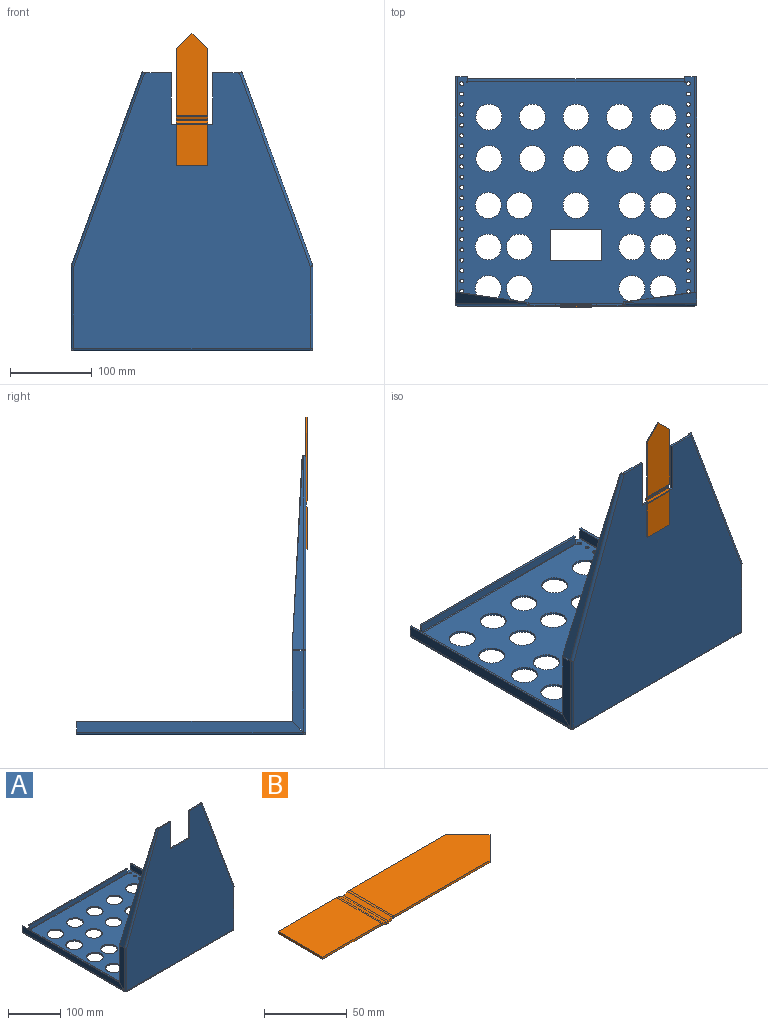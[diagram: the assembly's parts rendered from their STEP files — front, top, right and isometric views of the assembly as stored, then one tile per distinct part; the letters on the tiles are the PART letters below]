
ASSEMBLY  parts=2 mates=1
PART A: 171 faces, bbox 295.7x280.2x341.3 mm
  f0: plane 2.54x0.01mm, normal (0,1,0), area 0mm2, adj f15,f16,f26,f30
  f1: plane 2.54x0.01mm, normal (0,0,-1), area 0mm2, adj f30,f35,f36,f37
  f2: plane 2.54x0.01mm, normal (0,1,0), area 0mm2, adj f15,f16,f25,f31
  f3: plane 2.54x0.01mm, normal (0,0,-1), area 0mm2, adj f31,f34,f36,f37
  f4: plane 236.89x86.82mm, normal (-0.94,0,0.34), area 1788.3mm2, adj f6,f7,f97,f99,f170
  f5: plane 236.89x86.82mm, normal (0.94,0,-0.34), area 1788.3mm2, adj f6,f7,f98,f99,f170
  f6: plane 8.51x5.18mm, normal (0,1,0), area 20.6mm2, adj f4,f5,f99,f170
  f7: plane 2.39x0.87mm, normal (0.34,0,0.94), area 1.4mm2, adj f4,f5,f96,f170
  f8: plane 2.39x1.27mm, normal (-0.34,0,0.94), area 3.2mm2, adj f9,f10,f63,f169
  f9: plane 236.89x86.82mm, normal (0.94,0,0.34), area 1878.2mm2, adj f8,f11,f65,f67,f169
  f10: plane 236.89x86.82mm, normal (-0.94,0,-0.34), area 1878.2mm2, adj f8,f11,f66,f67,f169
  f11: plane 8.51x5.18mm, normal (0,1,0), area 20.6mm2, adj f9,f10,f67,f169
  f12: plane 337.08x289.1mm, normal (0,-1,0), area 73613.6mm2, adj f14,f18,f41,f43,f44,f45,f47,f48
  f13: plane 337.08x289.1mm, normal (0,1,0), area 73613.6mm2, adj f14,f18,f42,f43,f44,f45,f47,f48
  f14: plane 30.88x2.54mm, normal (0,0,1), area 78.4mm2, adj f12,f13,f45,f53
  f15: plane 289.1x276.89mm, normal (0,0,-1), area 57101.5mm2, adj f0,f2,f17,f19,f20,f21,f22,f23
  f16: plane 289.1x276.89mm, normal (0,0,1), area 57101.5mm2, adj f0,f2,f17,f19,f20,f21,f22,f23
  f17: plane 11.96x2.54mm, normal (0,1,0), area 30.4mm2, adj f15,f16,f21,f69
  f18: plane 30.88x2.54mm, normal (0,0,1), area 78.4mm2, adj f12,f13,f44,f48
  f19: plane 11.96x2.54mm, normal (0,1,0), area 30.4mm2, adj f15,f16,f20,f77
  f20: plane 5.08x2.54mm, normal (1,0,0), area 12.9mm2, adj f15,f16,f19,f22
  f21: plane 5.08x2.54mm, normal (-1,0,0), area 12.9mm2, adj f15,f16,f17,f29
  f22: plane 2.54x1.27mm, normal (0,-1,0), area 3.2mm2, adj f15,f16,f20,f23
  f23: plane 2.54x2.01mm, normal (1,0,0), area 5.1mm2, adj f15,f16,f22,f24
  f24: plane 2.54x1.27mm, normal (0,1,0), area 3.2mm2, adj f15,f16,f23,f25
  f25: plane 2.54x1.27mm, normal (-1,0,0), area 3.2mm2, adj f2,f15,f16,f24
  f26: plane 2.54x1.27mm, normal (1,0,0), area 3.2mm2, adj f0,f15,f16,f27
  f27: plane 2.54x1.27mm, normal (0,1,0), area 3.2mm2, adj f15,f16,f26,f28
  f28: plane 2.54x2.01mm, normal (-1,0,0), area 5.1mm2, adj f15,f16,f27,f29
  f29: plane 2.54x1.27mm, normal (0,-1,0), area 3.2mm2, adj f15,f16,f21,f28
  f30: plane 3.28x3.28mm, normal (1,0,0), area 8mm2, adj f0,f1,f32,f33
  f31: plane 3.28x3.28mm, normal (-1,0,0), area 8mm2, adj f2,f3,f32,f33
  f32: cylinder r=3.28mm len=265.16mm, axis (-1,0,0), area 1364.7mm2, adj f15,f30,f31,f36
  f33: cylinder r=0.74mm len=265.16mm, axis (-1,0,0), area 306.8mm2, adj f16,f30,f31,f37
  f34: plane 10.19x2.54mm, normal (-1,0,0), area 25.9mm2, adj f3,f36,f37,f38
  f35: plane 10.19x2.54mm, normal (1,0,0), area 25.9mm2, adj f1,f36,f37,f38
  f36: plane 265.18x10.19mm, normal (0,1,0), area 2700.9mm2, adj f1,f3,f32,f34,f35,f38
  f37: plane 265.18x10.19mm, normal (0,-1,0), area 2700.9mm2, adj f1,f3,f33,f34,f35,f38
  f38: plane 265.18x2.54mm, normal (0,0,1), area 673.5mm2, adj f34,f35,f36,f37
  f39: plane 3.28x3.28mm, normal (-1,0,0), area 8mm2, adj f41,f42,f50,f51
  f40: plane 3.28x3.28mm, normal (1,0,0), area 8mm2, adj f41,f42,f46,f49
  f41: cylinder r=3.28mm len=290.58mm, axis (1,0,0), area 1495.6mm2, adj f12,f15,f39,f40,f46,f49,f50,f51
  f42: cylinder r=0.74mm len=290.58mm, axis (1,0,0), area 336.2mm2, adj f13,f16,f39,f40,f46,f49,f50,f51
  f43: plane 50.8x2.54mm, normal (0,0,1), area 129mm2, adj f12,f13,f44,f45
  f44: plane 63.5x2.54mm, normal (-1,0,0), area 161.3mm2, adj f12,f13,f18,f43
  f45: plane 63.5x2.54mm, normal (1,0,0), area 161.3mm2, adj f12,f13,f14,f43
  f46: plane 2.54x0.74mm, normal (0,0,1), area 1.9mm2, adj f40,f41,f42,f55
  f47: plane 2.54x1.19mm, normal (-0.34,0,0.94), area 3.2mm2, adj f12,f13,f48,f63
  f48: plane 2.54x0.69mm, normal (0.94,0,0.34), area 1.9mm2, adj f12,f13,f18,f47
  f49: plane 2.54x0.74mm, normal (0,1,0), area 1.9mm2, adj f40,f41,f42,f68
  f50: plane 2.54x0.74mm, normal (0,1,0), area 1.9mm2, adj f39,f41,f42,f78
  f51: plane 2.54x0.74mm, normal (0,0,1), area 1.9mm2, adj f39,f41,f42,f86
  f52: plane 2.54x1.19mm, normal (0.34,0,0.94), area 3.2mm2, adj f12,f13,f53,f96
  f53: plane 2.54x0.69mm, normal (-0.94,0,0.34), area 1.9mm2, adj f12,f13,f14,f52
  f54: plane 3.28x3.28mm, normal (0,0,1), area 8mm2, adj f56,f57,f61,f64
  f55: bspline ~3.3x3.3mm, area 8mm2, adj f46,f56,f57,f62
  f56: cylinder r=3.28mm len=99.95mm, axis (0,0,-1), area 513.9mm2, adj f12,f54,f55,f58
  f57: cylinder r=0.74mm len=99.95mm, axis (0,0,-1), area 115.5mm2, adj f13,f54,f55,f59
  f58: plane 99.77x13.23mm, normal (1,0,0), area 1232.7mm2, adj f56,f60,f61,f62
  f59: plane 99.77x13.23mm, normal (-1,0,0), area 1232.7mm2, adj f57,f60,f61,f62
  f60: plane 86.53x2.54mm, normal (0,1,0), area 219.8mm2, adj f58,f59,f61,f62
  f61: plane 13.23x2.54mm, normal (0,0,1), area 33.6mm2, adj f54,f58,f59,f60
  f62: plane 13.23x13.23mm, normal (0,0.71,-0.71), area 47.5mm2, adj f55,f58,f59,f60
  f63: plane 3.28x3.08mm, normal (-0.34,0,0.94), area 8mm2, adj f8,f47,f65,f66
  f64: plane 3.28x3.08mm, normal (0.34,0,-0.94), area 8mm2, adj f54,f65,f66,f67
  f65: cylinder r=3.28mm len=238.01mm, axis (0.34,0,-0.94), area 1298.5mm2, adj f9,f12,f63,f64
  f66: cylinder r=0.74mm len=237.14mm, axis (0.34,0,-0.94), area 291.9mm2, adj f10,f13,f63,f64
  f67: plane 13.23x2.39mm, normal (0.34,0,-0.94), area 33.6mm2, adj f9,f10,f11,f64
  f68: bspline ~3.3x3.3mm, area 8mm2, adj f49,f70,f71,f76
  f69: plane 3.28x3.28mm, normal (0,1,0), area 8mm2, adj f17,f70,f71,f75
  f70: cylinder r=3.28mm len=276.89mm, axis (0,1,0), area 1424.6mm2, adj f15,f68,f69,f72
  f71: cylinder r=0.74mm len=276.89mm, axis (0,1,0), area 320.3mm2, adj f16,f68,f69,f73
  f72: plane 276.71x13.23mm, normal (1,0,0), area 3574.2mm2, adj f70,f74,f75,f76
  f73: plane 276.71x13.23mm, normal (-1,0,0), area 3574.2mm2, adj f71,f74,f75,f76
  f74: plane 263.47x2.54mm, normal (0,0,1), area 669.2mm2, adj f72,f73,f75,f76
  f75: plane 13.23x2.54mm, normal (0,1,0), area 33.6mm2, adj f69,f72,f73,f74
  f76: plane 13.23x13.23mm, normal (0,-0.71,0.71), area 47.5mm2, adj f68,f72,f73,f74
  f77: plane 3.28x3.28mm, normal (0,1,0), area 8mm2, adj f19,f79,f80,f84
  f78: bspline ~3.3x3.3mm, area 8mm2, adj f50,f79,f80,f85
  f79: cylinder r=3.28mm len=276.89mm, axis (0,-1,0), area 1424.6mm2, adj f15,f77,f78,f81
  f80: cylinder r=0.74mm len=276.89mm, axis (0,-1,0), area 320.3mm2, adj f16,f77,f78,f82
  f81: plane 276.71x13.23mm, normal (-1,0,0), area 3574.2mm2, adj f79,f83,f84,f85
  f82: plane 276.71x13.23mm, normal (1,0,0), area 3574.2mm2, adj f80,f83,f84,f85
  f83: plane 263.47x2.54mm, normal (0,0,1), area 669.2mm2, adj f81,f82,f84,f85
  f84: plane 13.23x2.54mm, normal (0,1,0), area 33.6mm2, adj f77,f81,f82,f83
  f85: plane 13.23x13.23mm, normal (0,-0.71,0.71), area 47.5mm2, adj f78,f81,f82,f83
  f86: bspline ~3.3x3.3mm, area 8mm2, adj f51,f88,f89,f94
  f87: plane 3.28x3.28mm, normal (0,0,1), area 8mm2, adj f88,f89,f93,f95
  f88: cylinder r=3.28mm len=99.95mm, axis (0,0,1), area 513.9mm2, adj f12,f86,f87,f90
  f89: cylinder r=0.74mm len=99.95mm, axis (0,0,1), area 115.5mm2, adj f13,f86,f87,f91
  f90: plane 99.77x13.23mm, normal (-1,0,0), area 1232.7mm2, adj f88,f92,f93,f94
  f91: plane 99.77x13.23mm, normal (1,0,0), area 1232.7mm2, adj f89,f92,f93,f94
  f92: plane 86.53x2.54mm, normal (0,1,0), area 219.8mm2, adj f90,f91,f93,f94
  f93: plane 13.23x2.54mm, normal (0,0,1), area 33.6mm2, adj f87,f90,f91,f92
  f94: plane 13.23x13.23mm, normal (0,0.71,-0.71), area 47.5mm2, adj f86,f90,f91,f92
  f95: plane 3.28x3.08mm, normal (-0.34,0,-0.94), area 8mm2, adj f87,f97,f98,f99
  f96: plane 3.28x3.08mm, normal (0.34,0,0.94), area 8mm2, adj f7,f52,f97,f98
  f97: cylinder r=3.28mm len=238.01mm, axis (0.34,0,0.94), area 1298.5mm2, adj f4,f12,f95,f96
  f98: cylinder r=0.74mm len=237.14mm, axis (0.34,0,0.94), area 291.9mm2, adj f5,f13,f95,f96
  f99: plane 13.23x2.39mm, normal (-0.34,0,-0.94), area 33.6mm2, adj f4,f5,f6,f95
  f100: plane 38.1x2.54mm, normal (-1,0,0), area 96.8mm2, adj f15,f16,f101,f103
  f101: plane 63.55x2.54mm, normal (0,1,0), area 161.4mm2, adj f15,f16,f100,f102
  f102: plane 38.1x2.54mm, normal (1,0,0), area 96.8mm2, adj f15,f16,f101,f103
  f103: plane 63.55x2.54mm, normal (0,-1,0), area 161.4mm2, adj f15,f16,f100,f102
  f104: cylinder r=2.41mm len=4.83mm, axis (0,0,1), area 38.5mm2, adj f15,f16
  f105: cylinder r=2.41mm len=4.83mm, axis (0,0,1), area 38.5mm2, adj f15,f16
  f106: cylinder r=2.41mm len=4.83mm, axis (0,0,1), area 38.5mm2, adj f15,f16
  f107: cylinder r=2.41mm len=4.83mm, axis (0,0,1), area 38.5mm2, adj f15,f16
  f108: cylinder r=2.41mm len=4.83mm, axis (0,0,1), area 38.5mm2, adj f15,f16
  f109: cylinder r=2.41mm len=4.83mm, axis (0,0,1), area 38.5mm2, adj f15,f16
  f110: cylinder r=2.41mm len=4.83mm, axis (0,0,1), area 38.5mm2, adj f15,f16
  f111: cylinder r=2.41mm len=4.83mm, axis (0,0,1), area 38.5mm2, adj f15,f16
  f112: cylinder r=2.41mm len=4.83mm, axis (0,0,1), area 38.5mm2, adj f15,f16
  f113: cylinder r=2.41mm len=4.83mm, axis (0,0,1), area 38.5mm2, adj f15,f16
  f114: cylinder r=2.41mm len=4.83mm, axis (0,0,1), area 38.5mm2, adj f15,f16
  f115: cylinder r=2.41mm len=4.83mm, axis (0,0,1), area 38.5mm2, adj f15,f16
  f116: cylinder r=2.41mm len=4.83mm, axis (0,0,1), area 38.5mm2, adj f15,f16
  f117: cylinder r=2.41mm len=4.83mm, axis (0,0,1), area 38.5mm2, adj f15,f16
  f118: cylinder r=2.41mm len=4.83mm, axis (0,0,1), area 38.5mm2, adj f15,f16
  f119: cylinder r=2.41mm len=4.83mm, axis (0,0,1), area 38.5mm2, adj f15,f16
  f120: cylinder r=2.41mm len=4.83mm, axis (0,0,1), area 38.5mm2, adj f15,f16
  f121: cylinder r=2.41mm len=4.83mm, axis (0,0,1), area 38.5mm2, adj f15,f16
  f122: cylinder r=2.41mm len=4.83mm, axis (0,0,1), area 38.5mm2, adj f15,f16
  f123: cylinder r=2.41mm len=4.83mm, axis (0,0,1), area 38.5mm2, adj f15,f16
  f124: cylinder r=2.41mm len=4.83mm, axis (0,0,1), area 38.5mm2, adj f15,f16
  f125: cylinder r=2.41mm len=4.83mm, axis (0,0,1), area 38.5mm2, adj f15,f16
  f126: cylinder r=2.41mm len=4.83mm, axis (0,0,1), area 38.5mm2, adj f15,f16
  f127: cylinder r=2.41mm len=4.83mm, axis (0,0,1), area 38.5mm2, adj f15,f16
  f128: cylinder r=2.41mm len=4.83mm, axis (0,0,1), area 38.5mm2, adj f15,f16
  f129: cylinder r=2.41mm len=4.83mm, axis (0,0,1), area 38.5mm2, adj f15,f16
  f130: cylinder r=2.41mm len=4.83mm, axis (0,0,1), area 38.5mm2, adj f15,f16
  f131: cylinder r=2.41mm len=4.83mm, axis (0,0,1), area 38.5mm2, adj f15,f16
  f132: cylinder r=2.41mm len=4.83mm, axis (0,0,1), area 38.5mm2, adj f15,f16
  f133: cylinder r=2.41mm len=4.83mm, axis (0,0,1), area 38.5mm2, adj f15,f16
  f134: cylinder r=2.41mm len=4.83mm, axis (0,0,1), area 38.5mm2, adj f15,f16
  f135: cylinder r=2.41mm len=4.83mm, axis (0,0,1), area 38.5mm2, adj f15,f16
  f136: cylinder r=2.41mm len=4.83mm, axis (0,0,1), area 38.5mm2, adj f15,f16
  f137: cylinder r=2.41mm len=4.83mm, axis (0,0,1), area 38.5mm2, adj f15,f16
  f138: cylinder r=2.41mm len=4.83mm, axis (0,0,1), area 38.5mm2, adj f15,f16
  f139: cylinder r=2.41mm len=4.83mm, axis (0,0,1), area 38.5mm2, adj f15,f16
  f140: cylinder r=2.41mm len=4.83mm, axis (0,0,1), area 38.5mm2, adj f15,f16
  f141: cylinder r=2.41mm len=4.83mm, axis (0,0,1), area 38.5mm2, adj f15,f16
  f142: cylinder r=2.41mm len=4.83mm, axis (0,0,1), area 38.5mm2, adj f15,f16
  f143: cylinder r=2.41mm len=4.83mm, axis (0,0,1), area 38.5mm2, adj f15,f16
  f144: cylinder r=2.41mm len=4.83mm, axis (0,0,1), area 38.5mm2, adj f15,f16
  f145: cylinder r=2.41mm len=4.83mm, axis (0,0,1), area 38.5mm2, adj f15,f16
  f146: cylinder r=15.88mm len=31.75mm, axis (0,0,1), area 253.4mm2, adj f15,f16
  f147: cylinder r=15.88mm len=31.75mm, axis (0,0,1), area 253.4mm2, adj f15,f16
  f148: cylinder r=15.88mm len=31.75mm, axis (0,0,1), area 253.4mm2, adj f15,f16
  f149: cylinder r=15.88mm len=31.75mm, axis (0,0,1), area 253.4mm2, adj f15,f16
  f150: cylinder r=15.88mm len=31.75mm, axis (0,0,1), area 253.4mm2, adj f15,f16
  f151: cylinder r=15.88mm len=31.75mm, axis (0,0,1), area 253.4mm2, adj f15,f16
  f152: cylinder r=15.88mm len=31.75mm, axis (0,0,1), area 253.4mm2, adj f15,f16
  f153: cylinder r=15.88mm len=31.75mm, axis (0,0,1), area 253.4mm2, adj f15,f16
  f154: cylinder r=15.88mm len=31.75mm, axis (0,0,1), area 253.4mm2, adj f15,f16
  f155: cylinder r=15.88mm len=31.75mm, axis (0,0,1), area 253.4mm2, adj f15,f16
  f156: cylinder r=15.88mm len=31.75mm, axis (0,0,1), area 253.4mm2, adj f15,f16
  f157: cylinder r=15.88mm len=31.75mm, axis (0,0,1), area 253.4mm2, adj f15,f16
  f158: cylinder r=15.88mm len=31.75mm, axis (0,0,1), area 253.4mm2, adj f15,f16
  f159: cylinder r=15.88mm len=31.75mm, axis (0,0,1), area 253.4mm2, adj f15,f16
  f160: cylinder r=15.88mm len=31.75mm, axis (0,0,1), area 253.4mm2, adj f15,f16
  f161: cylinder r=15.88mm len=31.75mm, axis (0,0,1), area 253.4mm2, adj f15,f16
  f162: cylinder r=15.88mm len=31.75mm, axis (0,0,1), area 253.4mm2, adj f15,f16
  f163: cylinder r=15.88mm len=31.75mm, axis (0,0,1), area 253.4mm2, adj f15,f16
  f164: cylinder r=15.88mm len=31.75mm, axis (0,0,1), area 253.4mm2, adj f15,f16
  f165: cylinder r=15.88mm len=31.75mm, axis (0,0,1), area 253.4mm2, adj f15,f16
  f166: cylinder r=15.88mm len=31.75mm, axis (0,0,1), area 253.4mm2, adj f15,f16
  f167: cylinder r=15.88mm len=31.75mm, axis (0,0,1), area 253.4mm2, adj f15,f16
  f168: cylinder r=15.88mm len=31.75mm, axis (0,0,1), area 253.4mm2, adj f15,f16
  f169: plane 230.13x86.41mm, normal (-0.02,1,0.05), area 620.9mm2, adj f8,f9,f10,f11
  f170: plane 230.13x86.41mm, normal (0.02,1,0.05), area 621mm2, adj f4,f5,f6,f7
PART B: 31 faces, bbox 161.9x38.1x3.2 mm
  f0: plane 82.15x1.59mm, normal (0,1,0), area 130.4mm2, adj f2,f3,f4,f27
  f1: plane 82.15x1.59mm, normal (0,-1,0), area 130.4mm2, adj f2,f3,f5,f28
  f2: plane 101.2x38.1mm, normal (0,0,1), area 3492.7mm2, adj f0,f1,f4,f5,f29
  f3: plane 101.2x38.1mm, normal (0,0,-1), area 3492.7mm2, adj f0,f1,f4,f5,f30
  f4: plane 19.05x19.05mm, normal (0.71,0.71,0), area 42.8mm2, adj f0,f2,f3,f5
  f5: plane 19.05x19.05mm, normal (0.71,-0.71,0), area 42.8mm2, adj f1,f2,f3,f4
  f6: plane 3.89x2.71mm, normal (0,-1,0), area 5.7mm2, adj f8,f9,f23,f28
  f7: plane 3.89x2.71mm, normal (0,1,0), area 5.7mm2, adj f8,f9,f24,f27
  f8: plane 38.1x3.35mm, normal (-0.34,0,0.94), area 135.8mm2, adj f6,f7,f26,f29
  f9: plane 38.1x3.35mm, normal (0.34,0,-0.94), area 135.8mm2, adj f6,f7,f25,f30
  f10: plane 3.61x2.61mm, normal (0,-1,0), area 5.2mm2, adj f12,f13,f20,f23
  f11: plane 3.61x2.61mm, normal (0,1,0), area 5.2mm2, adj f12,f13,f19,f24
  f12: plane 38.1x3.07mm, normal (0.34,0,0.94), area 124.5mm2, adj f10,f11,f21,f26
  f13: plane 38.1x3.07mm, normal (-0.34,0,-0.94), area 124.5mm2, adj f10,f11,f22,f25
  f14: plane 38.1x1.59mm, normal (-1,0,0), area 60.5mm2, adj f15,f16,f17,f18
  f15: plane 50.12x1.59mm, normal (0,-1,0), area 79.6mm2, adj f14,f17,f18,f20
  f16: plane 50.12x1.59mm, normal (0,1,0), area 79.6mm2, adj f14,f17,f18,f19
  f17: plane 50.12x38.1mm, normal (0,0,1), area 1909.5mm2, adj f14,f15,f16,f21
  f18: plane 50.12x38.1mm, normal (0,0,-1), area 1909.5mm2, adj f14,f15,f16,f22
  f19: plane 1.73x1.33mm, normal (0,1,0), area 1.7mm2, adj f11,f16,f21,f22
  f20: plane 1.73x1.33mm, normal (0,-1,0), area 1.7mm2, adj f10,f15,f21,f22
  f21: cylinder r=3.87mm len=38.1mm, axis (0,1,0), area 51.5mm2, adj f12,f17,f19,f20
  f22: cylinder r=2.29mm len=38.1mm, axis (0,1,0), area 30.4mm2, adj f13,f18,f19,f20
  f23: plane 2.65x1.73mm, normal (0,-1,0), area 3.4mm2, adj f6,f10,f25,f26
  f24: plane 2.65x1.73mm, normal (0,1,0), area 3.4mm2, adj f7,f11,f25,f26
  f25: cylinder r=3.87mm len=38.1mm, axis (0,-1,0), area 103mm2, adj f9,f13,f23,f24
  f26: cylinder r=2.29mm len=38.1mm, axis (0,-1,0), area 60.8mm2, adj f8,f12,f23,f24
  f27: plane 1.73x1.33mm, normal (0,1,0), area 1.7mm2, adj f0,f7,f29,f30
  f28: plane 1.73x1.33mm, normal (0,-1,0), area 1.7mm2, adj f1,f6,f29,f30
  f29: cylinder r=3.87mm len=38.1mm, axis (0,1,0), area 51.5mm2, adj f2,f8,f27,f28
  f30: cylinder r=2.29mm len=38.1mm, axis (0,1,0), area 30.4mm2, adj f3,f9,f27,f28
PLACE A t=(-117.29,-31.88,13.29)mm
PLACE B rot(axis=(0.58,-0.58,0.58),120deg) t=(47.05,-31.98,297.84)mm
MATE fastened B.f18 <-> A.f12  axis (0,1,0) through (28,-34.42,287.61)mm
